# Revit family: Terminal_Unit-Single_Duct-Titus-DESV-Rectangular
name_source: partatom
category: Mechanical Equipment
revit_build: Autodesk Revit MEP 2012 (Build: 20110916_2132(x64)
units: mm (PartAtom-declared; Revit-internal decimal feet)

## types (3) — shared parameters
Assembly Code = D3040100
A‏ir Terminal Material = Steel - Titus - Galvanized
Control Box Width = 0' - 6 1/2"
Description = Digital Single Duct Terminal Unit
ENGworks URL = http://www.ENGworks.com
Inlet Front Offset = 0' - 3 3/8"
Manufacturer = Titus
Product Page URL = http://www.titus-hvac.com
Series = DESV
URL = http://www.titus-hvac.com
Version = 1

## per-type parameters (varying)
| type | Control Box Front Offset | Control Box Height | Control Box Length | Inlet Duct Height | Inlet Duct Width | Inlet Height | Inlet Width | Maximum Air Flow | Minimum Air Flow | Nominal Inlet Height | Nominal Inlet Width | Nominal Outlet Height | Nominal Outlet Width | Overall Height | Overall Length | Unit Length | Unit Weight | Unit Width |
| DESV-40 | 0' - 5 3/8" | 1' - 4 7/8" | 1' - 6" | 16" | 24" | 16" | 24" | 7500 CFM | 1400 CFM | 16" | 24" | 18" | 38" | 1' - 6" | 1' - 8 3/8" | 1' - 3" | 74.00 lb | 3' - 2" |
| DESV-20 | 0' - 2 3/4" | 0' - 10 1/4" | 1' - 3 1/4" | 8" | 14" | 8" | 12" | 1800 CFM | 600 CFM | 8" | 14" | 10" | 16" | 0' - 10 1/4" | 1' - 6 7/8" | 1' - 3 1/2" | 49.00 lb | 1' - 4" |
| DESV-30 | 0' - 2 3/4" | 0' - 10 1/4" | 1' - 3 1/4" | 8" | 25" | 8" | 24" | 4000 CFM | 1400 CFM | 8" | 25" | 10" | 27" | 0' - 10 1/4" | 1' - 6 7/8" | 1' - 3 1/2" | 53.00 lb | 2' - 3 1/4" |

note: column(s) folded — value = type name in every type: Model

## geometry (parser evidence)
native form markers: Blend x4, Sweep x2
no freeform markers — native parametric forms only
